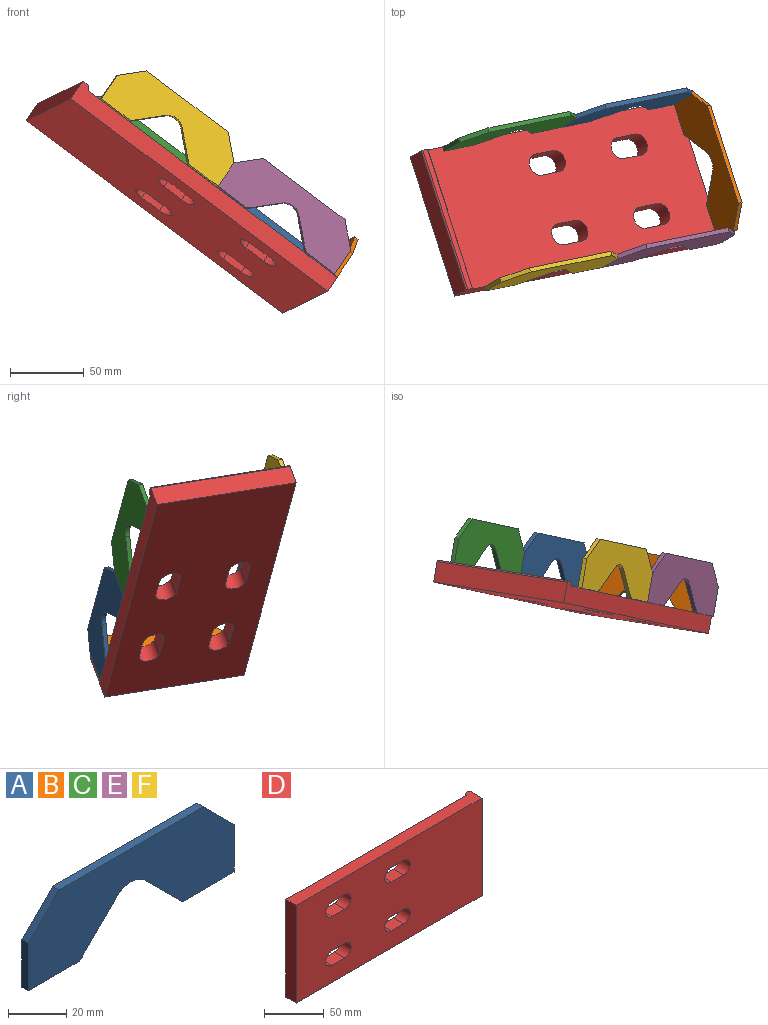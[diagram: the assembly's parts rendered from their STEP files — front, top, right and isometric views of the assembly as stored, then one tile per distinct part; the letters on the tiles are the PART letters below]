
ASSEMBLY  parts=6 mates=5
PART A: 14 faces, bbox 100x3x35 mm
  f0: cylinder r=10mm len=14.14mm, axis (0,1,0), area 47.1mm2, adj f1,f11,f12,f13
  f1: plane 17.05x17.05mm, normal (-0.71,0,-0.71), area 72.3mm2, adj f0,f2,f12,f13
  f2: cylinder r=3mm len=3mm, axis (0,1,0), area 7.1mm2, adj f1,f3,f12,f13
  f3: plane 23.76x3mm, normal (0,0,-1), area 71.3mm2, adj f2,f4,f12,f13
  f4: plane 20x3mm, normal (1,0,0), area 60mm2, adj f3,f5,f12,f13
  f5: plane 15x15mm, normal (0.71,0,0.71), area 63.6mm2, adj f4,f6,f12,f13
  f6: plane 70x3mm, normal (0,0,1), area 210mm2, adj f5,f7,f12,f13
  f7: plane 15x15mm, normal (-0.71,0,0.71), area 63.6mm2, adj f6,f8,f12,f13
  f8: plane 20x3mm, normal (-1,0,0), area 60mm2, adj f7,f9,f12,f13
  f9: plane 23.76x3mm, normal (0,0,-1), area 71.3mm2, adj f8,f10,f12,f13
  f10: cylinder r=3mm len=3mm, axis (0,1,0), area 7.1mm2, adj f9,f11,f12,f13
  f11: plane 17.05x17.05mm, normal (0.71,0,-0.71), area 72.3mm2, adj f0,f10,f12,f13
  f12: plane 100x35mm, normal (0,-1,0), area 2671.1mm2, adj f0,f1,f2,f3,f4,f5,f6,f7
  f13: plane 100x35mm, normal (0,1,0), area 2671.1mm2, adj f0,f1,f2,f3,f4,f5,f6,f7
PART B: same geometry as A
PART C: same geometry as A
PART D: 26 faces, bbox 220x15x100 mm
  f0: plane 100x12mm, normal (-1,0,0), area 1200mm2, adj f1,f5,f6,f7
  f1: plane 220x100mm, normal (0,-1,0), area 20393.1mm2, adj f0,f2,f6,f7,f8,f9,f10,f11
  f2: plane 100x14mm, normal (1,0,0), area 1400mm2, adj f1,f6,f7,f25
  f3: plane 100x4mm, normal (0,1,0), area 400mm2, adj f4,f6,f7,f25
  f4: plane 100x2.45mm, normal (-0.86,0.51,0), area 284.4mm2, adj f3,f6,f7,f24
  f5: plane 212.7x100mm, normal (0,1,0), area 19662.9mm2, adj f0,f6,f7,f8,f9,f10,f11,f12
  f6: plane 220x15mm, normal (0,0,1), area 2663.3mm2, adj f0,f1,f2,f3,f4,f5,f24,f25
  f7: plane 220x15mm, normal (0,0,-1), area 2663.3mm2, adj f0,f1,f2,f3,f4,f5,f24,f25
  f8: cylinder r=7.5mm len=15mm, axis (0,1,0), area 283.1mm2, adj f1,f5,f9,f11
  f9: plane 15x12.01mm, normal (0,0,1), area 180.2mm2, adj f1,f5,f8,f10
  f10: cylinder r=7.5mm len=15mm, axis (0,1,0), area 283mm2, adj f1,f5,f9,f11
  f11: plane 15x12.01mm, normal (0,0,-1), area 180.2mm2, adj f1,f5,f8,f10
  f12: cylinder r=7.5mm len=15mm, axis (0,1,0), area 283.5mm2, adj f1,f5,f13,f15
  f13: plane 15x12.03mm, normal (0,0,1), area 180.5mm2, adj f1,f5,f12,f14
  f14: cylinder r=7.5mm len=15mm, axis (0,1,0), area 283.4mm2, adj f1,f5,f13,f15
  f15: plane 15x12.03mm, normal (0,0,-1), area 180.5mm2, adj f1,f5,f12,f14
  f16: cylinder r=7.5mm len=15mm, axis (0,1,0), area 283.5mm2, adj f1,f5,f17,f19
  f17: plane 15x12.03mm, normal (0,0,1), area 180.5mm2, adj f1,f5,f16,f18
  f18: cylinder r=7.5mm len=15mm, axis (0,1,0), area 283.4mm2, adj f1,f5,f17,f19
  f19: plane 15x12.03mm, normal (0,0,-1), area 180.5mm2, adj f1,f5,f16,f18
  f20: cylinder r=7.5mm len=15mm, axis (0,1,0), area 283.1mm2, adj f1,f5,f21,f23
  f21: plane 15x12.01mm, normal (0,0,1), area 180.2mm2, adj f1,f5,f20,f22
  f22: cylinder r=7.5mm len=15mm, axis (0,1,0), area 283mm2, adj f1,f5,f21,f23
  f23: plane 15x12.01mm, normal (0,0,-1), area 180.2mm2, adj f1,f5,f20,f22
  f24: cylinder r=1mm len=100mm, axis (0,0,-1), area 104mm2, adj f4,f5,f6,f7
  f25: cylinder r=1mm len=100mm, axis (0,0,-1), area 157.1mm2, adj f2,f3,f6,f7
PART E: same geometry as A
PART F: same geometry as A
PLACE A rot(axis=(-0.34,0.87,0.36),40.4deg) t=(-184.45,-36.24,80.54)mm
PLACE B rot(axis=(-0.45,0.19,-0.87),82.7deg) t=(-131.47,-74.11,59.01)mm
PLACE C rot(axis=(-0.34,0.87,0.36),40.4deg) t=(-263.42,-52.3,139.75)mm
PLACE D rot(axis=(-0.13,-0.78,-0.61),145.2deg) t=(-230.61,-99.81,98.14)mm
PLACE E rot(axis=(-0.34,0.87,0.36),40.4deg) t=(-156.56,-130.87,97.14)mm
PLACE F rot(axis=(-0.34,0.87,0.36),40.4deg) t=(-235.53,-146.93,156.35)mm
MATE planar B.f9 <-> D.f5  axis (-0.53,-0.3,-0.79) through (-152.35,-43.4,39.5)mm
MATE pin_slot B.f13 <-> D.f0  axis (0.79,0.16,-0.59) through (-124.5,-126.13,51.67)mm
MATE pin_slot E.f3 <-> B.f3  axis (0.53,0.3,0.79) through (-126.87,-126.61,53.45)mm
MATE pin_slot C.f3 <-> A.f9  axis (0.53,0.3,0.79) through (-233.73,-48.04,96.06)mm
MATE pin_slot C.f3 <-> D.f5  axis (-0.53,-0.3,-0.79) through (-233.73,-48.04,96.06)mm
